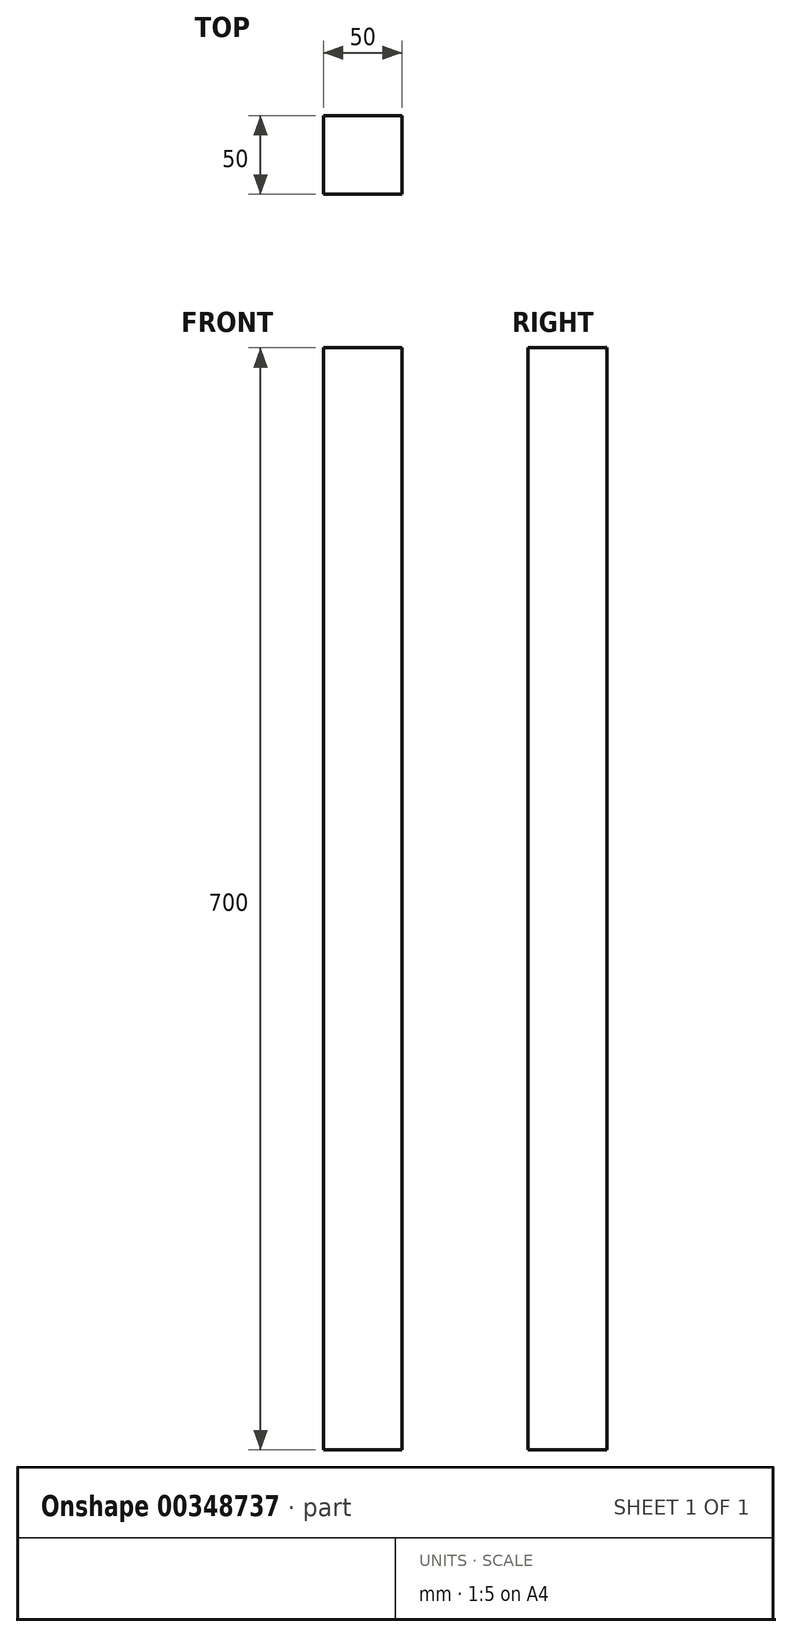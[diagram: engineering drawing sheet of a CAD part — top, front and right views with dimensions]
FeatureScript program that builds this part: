
annotation { "Feature Type Name" : "Feature", "Feature Type Description" : "" }
export const myFeature = defineFeature(function(context is Context, id is Id, definition is map)
    precondition{}
    {
        {
            var Q0;
            Q0=qCreatedBy(makeId("Top.planeOp"),FACE);
            var sketch = newSketch(context, id + "F0", { "sketchPlane" : qUnion([Q0])});
            skLineSegment(sketch, "E0.bottom", {"start": v(-13.52, -50.12) * mm, "end": v(-63.52, -50.12) * mm});
            skLineSegment(sketch, "E0.top", {"start": v(-13.52, -0.12) * mm, "end": v(-63.52, -0.12) * mm});
            skLineSegment(sketch, "E0.left", {"start": v(-13.52, -50.12) * mm, "end": v(-13.52, -0.12) * mm});
            skLineSegment(sketch, "E0.right", {"start": v(-63.52, -50.12) * mm, "end": v(-63.52, -0.12) * mm});
            skPoint(sketch, "E0.middle", {"position": v(-38.52, -25.12) * mm});
            skSolve(sketch);
        }
        {
            var Q0;
            Q0=makeQuery(id+"F0.imprint","IMPRINT",FACE,{"disambiguationData":[TD([[makeQuery(id+"F0.imprint","IMPRINT",EDGE,{"derivedFrom":sQuery(id+"F0.wireOp",EDGE,"E0.bottom")}),-1.0]])]});
            extrude(context, id + "F1", {"entities" : qUnion([Q0]), "depth" : 700 * mm});
        }
    });
